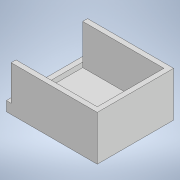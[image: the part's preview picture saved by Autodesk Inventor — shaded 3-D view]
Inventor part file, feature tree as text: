
AUTODESK INVENTOR PART (.ipt)
format: ipt  version: 2022 (Build 260153000, 153)  size: 105,472 bytes
history: native  units: mm
features: extrude x3, sketch x1
ambient origin geometry x8: Origin, YZ Plane, XZ Plane, XY Plane, X Axis, Y Axis, Z Axis, Center Point
bodies: Solid1 (feature_tree)
feature tree (4):
  sketch  "Sketch1"  dims[d0=67.0mm d1=55.0mm d2=4.0mm d3=33.0mm d4=0.0mm d5=4.0mm d6=0.0mm d7=4.0mm d8=0.0mm]
  extrude  "Extrusion1"  Depth=55.0mm
  extrude  "Extrusion2"  Depth=4.0mm
  extrude  "Extrusion3"  Depth=33.0mm TaperAngle=0.0deg
